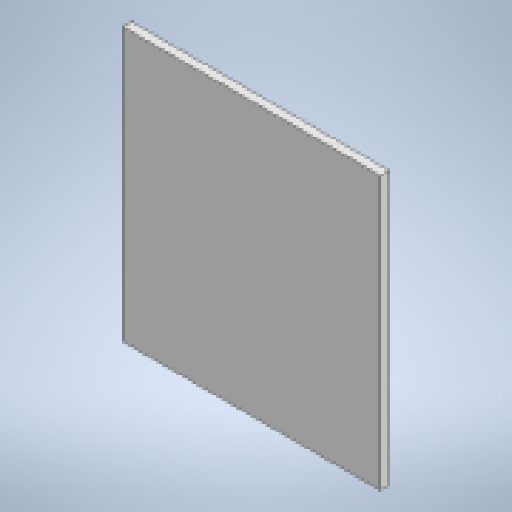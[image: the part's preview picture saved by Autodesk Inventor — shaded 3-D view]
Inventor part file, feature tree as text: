
AUTODESK INVENTOR PART (.ipt)
format: ipt  version: 2023 (Build 270158000, 158)  size: 158,720 bytes
history: native  units: in
note: dims shown in document units (in); Inventor stores cm internally (conversion verified against a paired STEP export)
features: other x7, extrude x3, sketch x3, reference x2, projected_geometry x2
ambient origin geometry x8: Origin, YZ Plane, XZ Plane, XY Plane, X Axis, Y Axis, Z Axis, Center Point
bodies: Body1 (feature_tree)
feature tree (17):
  other  "Bryła1"
  extrude  "Wyciągnięcie proste1"  Depth=0.063in TaperAngle=0.0deg
  other  "Płaszczyzna konstrukcyjna1"
  extrude  "Wyciągnięcie proste3"  Depth=0.6299in
  extrude  "Wyciągnięcie proste4"  Depth=0.6299in
  sketch  "Szkic1"
  reference  "Odniesienie1"
  sketch  "Szkic3"
  projected_geometry  "Pętla rzutowana2"
  sketch  "Szkic4"
  reference  "Odniesienie3"
  projected_geometry  "Pętla rzutowana3"
  other  "<userpath>\Documents\Inventor\MikroNalesnik\byk.iam"
  other  "byk.iam"
  other  "spod:1"
  other  "noz:1"
  other  "nozzz:1"
